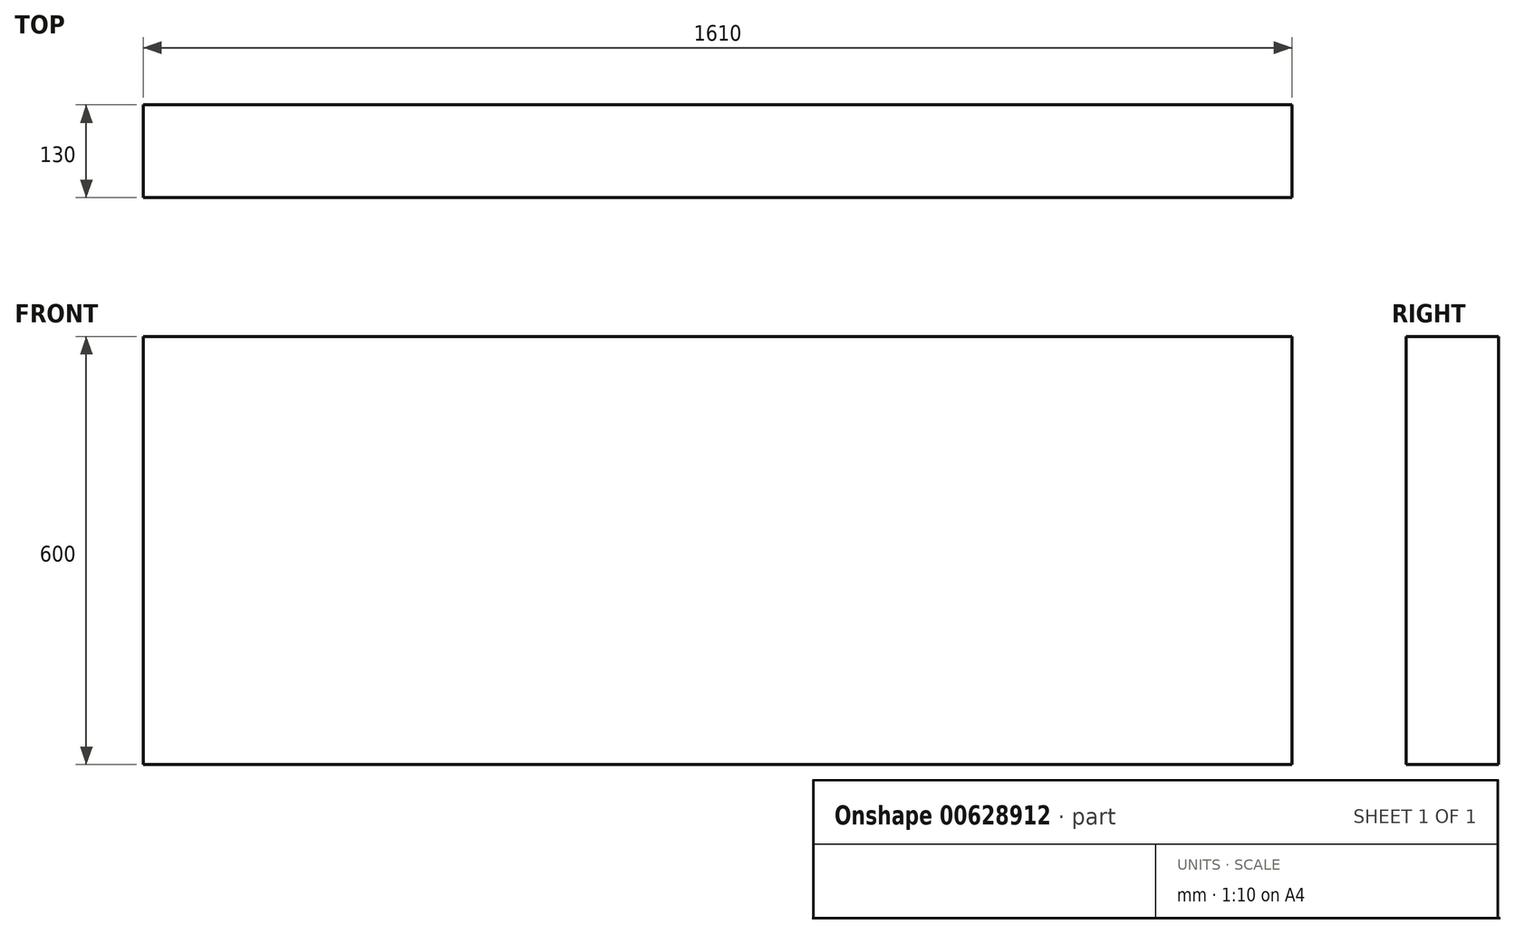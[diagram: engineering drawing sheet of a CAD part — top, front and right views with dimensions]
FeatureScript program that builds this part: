
annotation { "Feature Type Name" : "Feature", "Feature Type Description" : "" }
export const myFeature = defineFeature(function(context is Context, id is Id, definition is map)
    precondition{}
    {
        {
            var Q0;
            Q0=qCreatedBy(makeId("Front.planeOp"),FACE);
            var sketch = newSketch(context, id + "F0", { "sketchPlane" : qUnion([Q0])});
            skLineSegment(sketch, "E0.bottom", {"start": v(0, 0) * mm, "end": v(1610, 0) * mm});
            skLineSegment(sketch, "E0.top", {"start": v(0, 600) * mm, "end": v(1610, 600) * mm});
            skLineSegment(sketch, "E0.left", {"start": v(0, 0) * mm, "end": v(0, 600) * mm});
            skLineSegment(sketch, "E0.right", {"start": v(1610, 0) * mm, "end": v(1610, 600) * mm});
            skSolve(sketch);
        }
        {
            var Q0;
            Q0=makeQuery(id+"F0.imprint","IMPRINT",FACE,{"disambiguationData":[TD([[makeQuery(id+"F0.imprint","IMPRINT",EDGE,{"derivedFrom":sQuery(id+"F0.wireOp",EDGE,"E0.bottom")}),1.0]])]});
            extrude(context, id + "F1", {"entities" : qUnion([Q0]), "depth" : 130 * mm, "offsetDistance" : 25 * mm});
        }
    });
